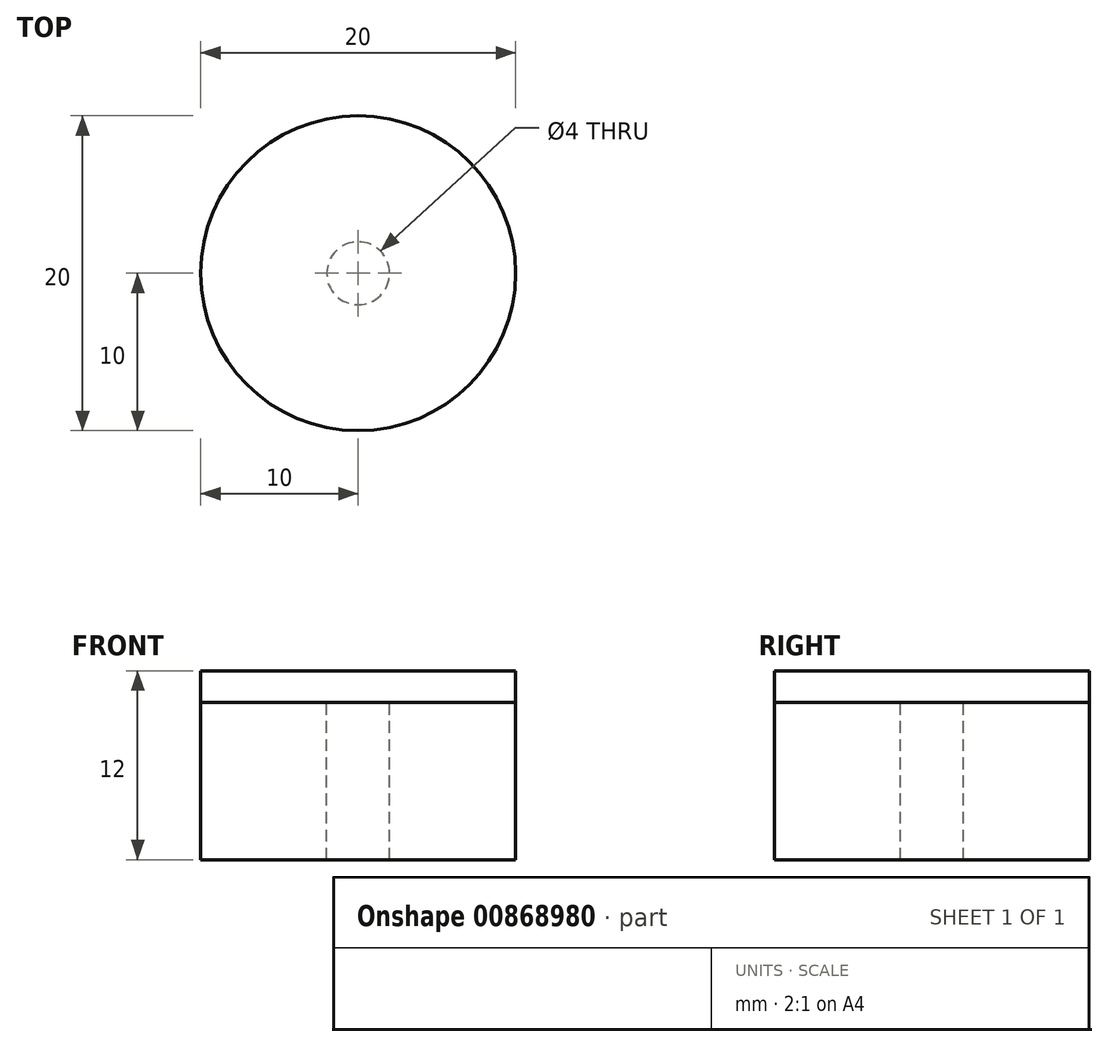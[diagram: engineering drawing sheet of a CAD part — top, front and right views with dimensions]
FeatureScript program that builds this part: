
annotation { "Feature Type Name" : "Feature", "Feature Type Description" : "" }
export const myFeature = defineFeature(function(context is Context, id is Id, definition is map)
    precondition{}
    {
        {
            var Q0;
            Q0=qCreatedBy(makeId("Front.planeOp"),FACE);
            var sketch = newSketch(context, id + "F0", { "sketchPlane" : qUnion([Q0])});
            skLineSegment(sketch, "E0", {"start": v(0, 0) * mm, "end": v(2, 0) * mm});
            skLineSegment(sketch, "E1", {"start": v(2, 0) * mm, "end": v(2, 10) * mm});
            skLineSegment(sketch, "E2", {"start": v(2, 10) * mm, "end": v(10, 10) * mm});
            skLineSegment(sketch, "E3", {"start": v(10, 10) * mm, "end": v(10, 12) * mm});
            skLineSegment(sketch, "E4", {"start": v(10, 12) * mm, "end": v(0, 12) * mm});
            skLineSegment(sketch, "E5", {"start": v(0, 12) * mm, "end": v(0, 0) * mm});
            skLineSegment(sketch, "E6", {"start": v(2, 0) * mm, "end": v(10, 0) * mm});
            skLineSegment(sketch, "E7", {"start": v(10, 0) * mm, "end": v(10, 10) * mm});
            skSolve(sketch);
        }
        {
            var Q0;
            Q0=makeQuery(id+"F0.imprint","IMPRINT",FACE,{"disambiguationData":[TD([[makeQuery(id+"F0.imprint","IMPRINT",EDGE,{"derivedFrom":sQuery(id+"F0.wireOp",EDGE,"E0")}),1.0]])]});
            var Q1;
            Q1=sQuery(id+"F0.wireOp",EDGE,"E5");
            revolve(context, id + "F1", {"surfaceOperationType" : NewSurfaceOperationType.NEW, "entities" : qUnion([Q0]), "axis" : qUnion([Q1]), "revolveType" : RevolveType.FULL});
        }
        {
            var Q0;
            Q0=makeQuery(id+"F0.imprint","IMPRINT",FACE,{"disambiguationData":[TD([[makeQuery(id+"F0.imprint","IMPRINT",EDGE,{"derivedFrom":sQuery(id+"F0.wireOp",EDGE,"E1")}),-1.0]])]});
            var Q1;
            Q1=sQuery(id+"F0.wireOp",EDGE,"E5");
            revolve(context, id + "F2", {"surfaceOperationType" : NewSurfaceOperationType.NEW, "entities" : qUnion([Q0]), "axis" : qUnion([Q1]), "revolveType" : RevolveType.FULL});
        }
    });
